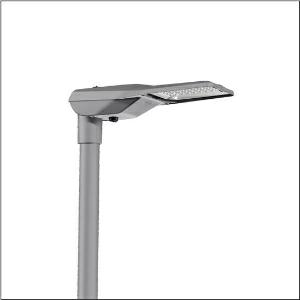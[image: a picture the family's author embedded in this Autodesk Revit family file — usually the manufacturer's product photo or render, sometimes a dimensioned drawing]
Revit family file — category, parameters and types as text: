
# Revit family: streetlight_sl_21_iq_mini___stw1_0a_5xe2e31y08jb_3a8f
name_source: partatom
category: Lighting Fixtures
units: mm (PartAtom-declared; Revit-internal decimal feet)

## family parameters
Cut with Voids When Loaded = No
Host = Face
Light Source = No
Part Type = Normal
Room Calculation Point = No
Round Connector Dimension = Use Diameter
Shared = No

## types (1)
- --- (1 x LED, 11210 lm, 72.5 W, 3000K)
    Apparent Load = 73 VA
    CIE Flux Codes = 39 75 98 100 100
    Color Rendering = 70
    Color Temperature = 3000K
    Default Elevation = 1800 mm
    Description = Streetlight SL 21 iQ mini, mast luminaire, primary light control with lens, of PMMA, primary optical cover: cover, of toughened safety glass, transparent, light distribution: STW1.0a, light emission: direct distribution, primary light characteristic: asymmetric, installation type: post-top, side-entry, LED, High Power LED, rated luminous flux: 11.210lm, luminous efficacy: 155lm/W, light colour: 730, colour temperature: 3000K, control: presetting dimming logarithmic, Street-Remote, Auto-Match, Temp-Guard, Lumen-Switch, Night-Set, Smart-Wire, Light-Fading, Desk-Remote (wireless, voltage-free reading and setting of iQ features in the workshop via application-optimized NFC function/RFID function), optimised constant luminous flux control (CLO 2.0), mains connection: 220..240V, AC, 50/60Hz, start of lifetime: 73W, end of service life: 76W, reduction: 33W, luminaire housing, of diecast aluminium, powder-coated, Siteco® metallic grey (DB 702S), corrosivity category C5 mid according to DIN EN ISO 12944, please order mast flange separately, inclination adjustable: 0°, 5°, 10°, 15°, sealing non-destructively replaceable, multi-level sealing system, length: 628mm, width: 235mm, height: 110mm, mast flange for spigot size: 42mm (side-entry): 5XC10008XM4, 60/48mm (side-entry/post-top): 5XC10108XM2, 76/60mm (side-entry/post-top): 5XC10108XM1, Smart Interface below and above, protection rating (complete): IP66, insulation class (complete): insulation class II (safety insulation), certification: CE, ENEC, ENEC+, VDE, impact resistance: IK09, permissible operating ambient temperature for outdoor applications: -40..+50°C, standard-compliant lighting for roads and squares, packaging unit: 1 piece

Light Distribution: STW1.0a
    Height = 110 mm
    Lamp = 1 x LED
    Lamp Light Flux = 11210 lm
    Lamp Power = 72.5 W
    Lamp count = 1
    Length = 625 mm
    Luminous efficacy = 155 lm/W
    Manufacturer = Siteco
    ModVariant = No
    Model = 5XE2E31Y08JB
    Number of Poles = 1
    OnlyDefault = Yes
    Power Factor = 1
    Product Name = Streetlight SL 21 iQ mini | STW1.0a
    Product group = mast luminaire | pylon top
    ProductGroupID = 6100
    Protection Class = Protection class II
    Protection Degree = IP 66
    RLX_Detail_Level = 1
    RLX_Emergency_Light_Flux = 0 lm
    RLX_Emergency_Type = 0
    RLX_Emergency_Type_DB = No
    RlxData = <blob elided: 92509 chars, md5=74789c03>
    Socket = socket
    Standby Power = 0 W
    System Light Flux = 11210 lm
    System Power = 73 W
    Type Comments = factory setting: luminous flux: 100 % | dim-lin: 254 | 755 mA
    Type Image = l_1003514.jpg
    URL = http://relux.com
    VarID = @adj_043731
    Voltage = 0 V
    Weight = 0.00 kg
    Width = 234 mm

## geometry (parser evidence)
native form markers: Blend x4, Sweep x10
no freeform markers — native parametric forms only
